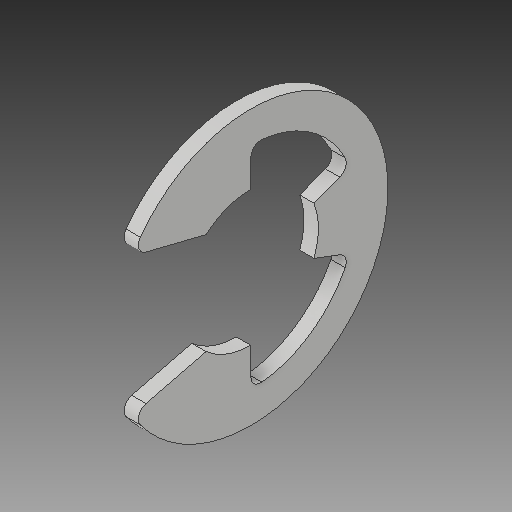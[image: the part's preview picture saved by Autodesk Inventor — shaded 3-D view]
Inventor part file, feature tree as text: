
AUTODESK INVENTOR PART (.ipt)
format: ipt  version: 2017 (Build 210142000, 142)  size: 114,688 bytes
history: native  units: in
note: dims shown in document units (in); Inventor stores cm internally (conversion verified against a paired STEP export)
features: fillet x1
ambient origin geometry x8: Origin, YZ Plane, XZ Plane, XY Plane, X Axis, Y Axis, Z Axis, Center Point
bodies: Solid1 (feature_tree)
feature tree (1):
  fillet  "Fillet1"  [1 undecoded]
note: 1 required parameter value undecoded (feature->parameter linkage not recoverable at this tier; creation-order binding heuristic only, values carry confidence <= 0.55)
